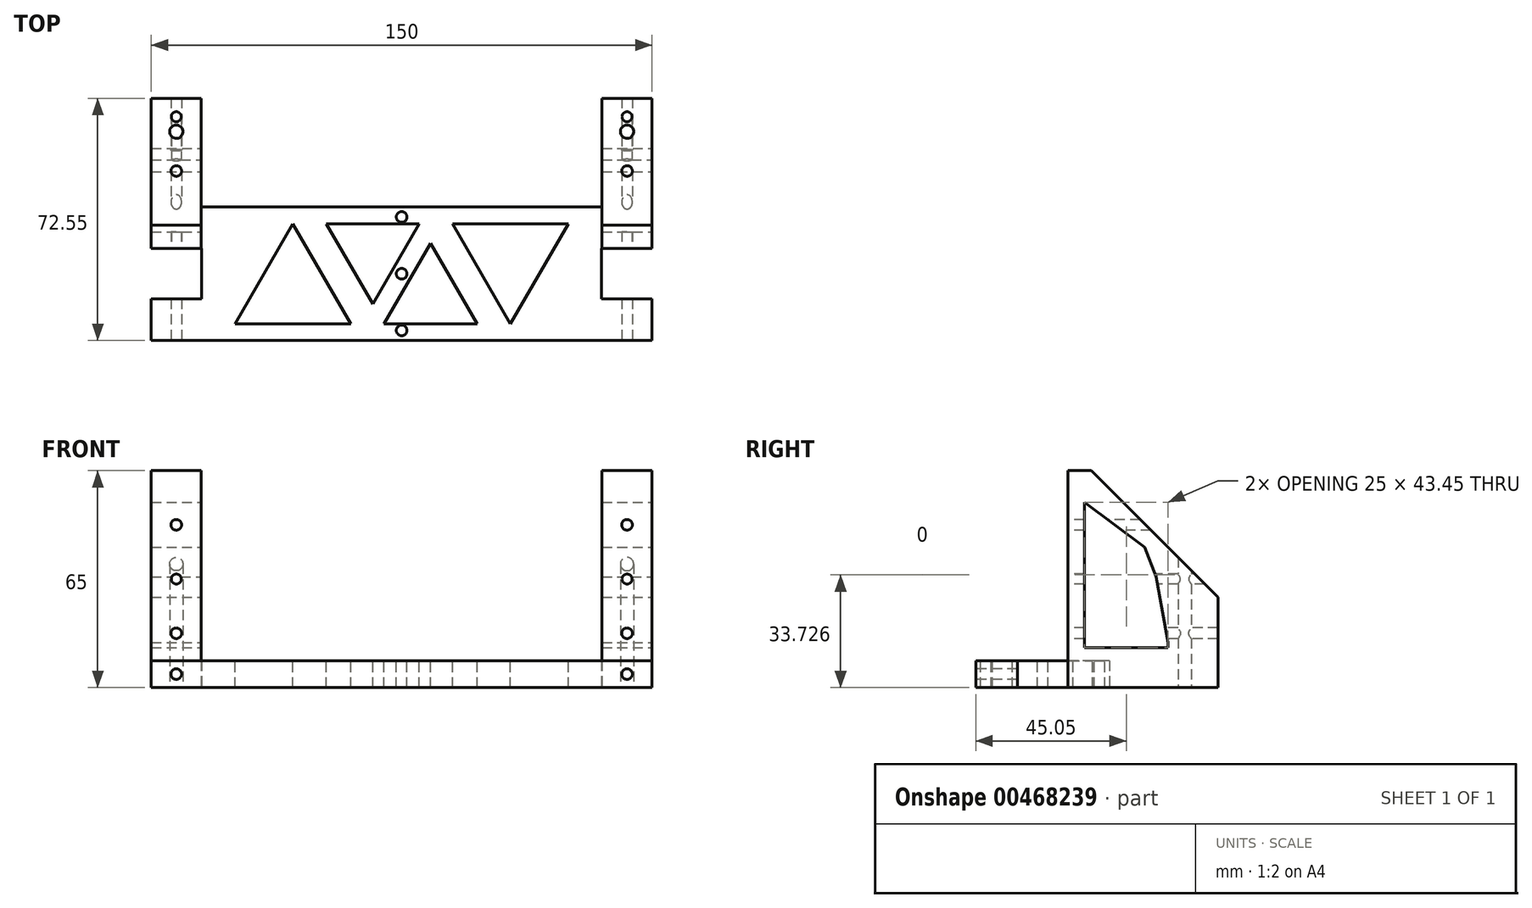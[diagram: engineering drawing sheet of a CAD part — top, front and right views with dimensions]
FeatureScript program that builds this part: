
annotation { "Feature Type Name" : "Feature", "Feature Type Description" : "" }
export const myFeature = defineFeature(function(context is Context, id is Id, definition is map)
    precondition{}
    {
        {
            var Q0;
            Q0=qCreatedBy(makeId("Top.planeOp"),FACE);
            var sketch = newSketch(context, id + "F0", { "sketchPlane" : qUnion([Q0])});
            skLineSegment(sketch, "E0.bottom", {"start": v(75, 20) * mm, "end": v(-75, 20) * mm});
            skLineSegment(sketch, "E0.top", {"start": v(75, -20) * mm, "end": v(-75, -20) * mm});
            skLineSegment(sketch, "E0.left", {"start": v(75, 20) * mm, "end": v(75, -20) * mm});
            skLineSegment(sketch, "E0.right", {"start": v(-75, 20) * mm, "end": v(-75, -20) * mm});
            skPoint(sketch, "E0.middle", {"position": v(0, 0) * mm});
            skLineSegment(sketch, "E1", {"start": v(-75, 0) * mm, "end": v(-67.45, 0) * mm});
            skLineSegment(sketch, "E2", {"start": v(75, 0) * mm, "end": v(67.45, 0) * mm});
            skLineSegment(sketch, "E3.bottom", {"start": v(75, 7.55) * mm, "end": v(59.9, 7.55) * mm});
            skLineSegment(sketch, "E3.top", {"start": v(75, -7.55) * mm, "end": v(59.9, -7.55) * mm});
            skLineSegment(sketch, "E3.left", {"start": v(75, 7.55) * mm, "end": v(75, -7.55) * mm});
            skLineSegment(sketch, "E3.right", {"start": v(59.9, 7.55) * mm, "end": v(59.9, -7.55) * mm});
            skPoint(sketch, "E3.middle", {"position": v(67.45, 0) * mm});
            skLineSegment(sketch, "E4.bottom", {"start": v(-59.9, 7.55) * mm, "end": v(-75, 7.55) * mm});
            skLineSegment(sketch, "E4.top", {"start": v(-59.9, -7.55) * mm, "end": v(-75, -7.55) * mm});
            skLineSegment(sketch, "E4.left", {"start": v(-59.9, 7.55) * mm, "end": v(-59.9, -7.55) * mm});
            skLineSegment(sketch, "E4.right", {"start": v(-75, 7.55) * mm, "end": v(-75, -7.55) * mm});
            skPoint(sketch, "E4.middle", {"position": v(-67.45, 0) * mm});
            skSolve(sketch);
        }
        {
            var Q0;
            {var subQ6=sQuery(id+"F0.wireOp",EDGE,"E0.bottom");Q0=makeQuery(id+"F0.imprint","IMPRINT",FACE,{"disambiguationData":[TD([[makeQuery(id+"F0.imprint","IMPRINT",EDGE,{"derivedFrom":subQ6}),1.0]])]});}
            extrude(context, id + "F1", {"entities" : qUnion([Q0]), "depth" : 8 * mm});
        }
        {
            var Q0;
            Q0=makeQuery(id+"F1.opExtrude","CAP_FACE",FACE,{"disambiguationData":[OSD([sQuery(id+"F0.wireOp",EDGE,"E0.bottom"),sQuery(id+"F0.wireOp",EDGE,"E0.top"),sQuery(id+"F0.wireOp",EDGE,"E0.left"),sQuery(id+"F0.wireOp",EDGE,"E0.right"),sQuery(id+"F0.wireOp",EDGE,"E3.bottom"),sQuery(id+"F0.wireOp",EDGE,"E3.top"),sQuery(id+"F0.wireOp",EDGE,"E3.right"),sQuery(id+"F0.wireOp",EDGE,"E4.bottom"),sQuery(id+"F0.wireOp",EDGE,"E4.top"),sQuery(id+"F0.wireOp",EDGE,"E4.left")])],"isStart":false});
            var sketch = newSketch(context, id + "F2", { "sketchPlane" : qUnion([Q0])});
            skLineSegment(sketch, "E5", {"start": v(0, 20) * mm, "end": v(0, 17) * mm});
            skPoint(sketch, "E5.endSnap0", {"position": v(0, 20) * mm});
            skLineSegment(sketch, "E6", {"start": v(0, -20) * mm, "end": v(0, -17) * mm});
            skPoint(sketch, "E6.endSnap0", {"position": v(0, -20) * mm});
            skCircle(sketch, "E7", {"center": v(0, -17) * mm, "radius": 1.6 * mm});
            skCircle(sketch, "E8", {"center": v(0, 0) * mm, "radius": 1.6 * mm});
            skCircle(sketch, "E9", {"center": v(0, 17) * mm, "radius": 1.6 * mm});
            skSolve(sketch);
        }
        {
            var Q0;
            Q0 = qSketchRegion(id + "F2", true);
            extrude(context, id + "F3", {"entities" : qUnion([Q0]), "operationType" : NewBodyOperationType.REMOVE, "oppositeDirection" : true, "depth" : 25 * mm});
        }
        {
            var Q0;
            Q0=makeQuery(id+"F1.opExtrude","CAP_FACE",FACE,{"disambiguationData":[OSD([sQuery(id+"F0.wireOp",EDGE,"E0.bottom"),sQuery(id+"F0.wireOp",EDGE,"E0.top"),sQuery(id+"F0.wireOp",EDGE,"E0.left"),sQuery(id+"F0.wireOp",EDGE,"E0.right"),sQuery(id+"F0.wireOp",EDGE,"E3.bottom"),sQuery(id+"F0.wireOp",EDGE,"E3.top"),sQuery(id+"F0.wireOp",EDGE,"E3.right"),sQuery(id+"F0.wireOp",EDGE,"E4.bottom"),sQuery(id+"F0.wireOp",EDGE,"E4.top"),sQuery(id+"F0.wireOp",EDGE,"E4.left")])],"isStart":true});
            var sketch = newSketch(context, id + "F4", { "sketchPlane" : qUnion([Q0])});
            skLineSegment(sketch, "E10.bottom", {"start": v(-75, -7.55) * mm, "end": v(-60, -7.55) * mm});
            skLineSegment(sketch, "E10.top", {"start": v(-75, -52.55) * mm, "end": v(-60, -52.55) * mm});
            skLineSegment(sketch, "E10.left", {"start": v(-75, -7.55) * mm, "end": v(-75, -52.55) * mm});
            skLineSegment(sketch, "E10.right", {"start": v(-60, -7.55) * mm, "end": v(-60, -52.55) * mm});
            skLineSegment(sketch, "E11.bottom", {"start": v(75, -7.55) * mm, "end": v(60, -7.55) * mm});
            skLineSegment(sketch, "E11.top", {"start": v(75, -52.55) * mm, "end": v(60, -52.55) * mm});
            skLineSegment(sketch, "E11.left", {"start": v(75, -7.55) * mm, "end": v(75, -52.55) * mm});
            skLineSegment(sketch, "E11.right", {"start": v(60, -7.55) * mm, "end": v(60, -52.55) * mm});
            skLineSegment(sketch, "E12", {"start": v(-67.5, -52.55) * mm, "end": v(-67.5, -42.55) * mm});
            skLineSegment(sketch, "E13", {"start": v(67.5, -52.55) * mm, "end": v(67.5, -42.55) * mm});
            skCircle(sketch, "E14", {"center": v(67.5, -42.55) * mm, "radius": 2 * mm});
            skCircle(sketch, "E15", {"center": v(-67.5, -42.55) * mm, "radius": 2 * mm});
            skSolve(sketch);
        }
        {
            var Q0;
            Q0=makeQuery(id+"F4.imprint","IMPRINT",FACE,{"disambiguationData":[TD([[makeQuery(id+"F4.imprint","IMPRINT",EDGE,{"derivedFrom":sQuery(id+"F4.wireOp",EDGE,"E15")}),-1.0]])]});
            var Q1;
            Q1=makeQuery(id+"F4.imprint","IMPRINT",FACE,{"disambiguationData":[TD([[makeQuery(id+"F4.imprint","IMPRINT",EDGE,{"derivedFrom":sQuery(id+"F4.wireOp",EDGE,"E14")}),-1.0]])]});
            var Q2;
            {var subQ0=sQuery(id+"F4.wireOp",EDGE,"E11.bottom");Q2=makeQuery(id+"F4.imprint","IMPRINT",FACE,{"disambiguationData":[TD([[makeQuery(id+"F4.imprint","IMPRINT",EDGE,{"derivedFrom":subQ0}),1.0]])]});}
            var Q3;
            {var subQ0=sQuery(id+"F4.wireOp",EDGE,"E10.bottom");Q3=makeQuery(id+"F4.imprint","IMPRINT",FACE,{"disambiguationData":[TD([[makeQuery(id+"F4.imprint","IMPRINT",EDGE,{"derivedFrom":subQ0}),1.0]])]});}
            extrude(context, id + "F5", {"entities" : qUnion([Q0, Q1, Q2, Q3]), "operationType" : NewBodyOperationType.ADD, "oppositeDirection" : true, "depth" : 65 * mm});
        }
        {
            var Q0;
            Q0=makeQuery(id+"F5.opExtrude","CAP_EDGE",EDGE,{"disambiguationData":[OSD([sQuery(id+"F4.wireOp",EDGE,"E11.top")])],"isStart":false});
            var Q1;
            Q1=makeQuery(id+"F5.opExtrude","CAP_EDGE",EDGE,{"disambiguationData":[OSD([sQuery(id+"F4.wireOp",EDGE,"E10.top")])],"isStart":false});
            chamfer(context, id + "F6", {"entities" : qUnion([Q0, Q1]), "width" : 38 * mm, "tangentPropagation" : true});
        }
        {
            var Q0;
            {var subQ0=sQuery(id+"F0.wireOp",EDGE,"E0.left");Q0=makeQuery(id+"F5.boolean.opBoolean","MERGE",FACE,{"derivedFrom":[makeQuery(id+"F1.opExtrude","SWEPT_FACE",FACE,{"disambiguationData":[OSD([subQ0]),TDD([makeQuery(id+"F0.imprint","IMPRINT",EDGE,{"disambiguationData":[TD([[makeQuery(id+"F0.imprint","INTERSECT",VERTEX,{"derivedFrom":[sQuery(id+"F0.wireOp",EDGE,"E0.bottom"),subQ0]}),-1.0]])],"derivedFrom":subQ0})])]}),makeQuery(id+"F5.opExtrude","SWEPT_FACE",FACE,{"disambiguationData":[OSD([sQuery(id+"F4.wireOp",EDGE,"E11.left")])]})]});}
            var sketch = newSketch(context, id + "F7", { "sketchPlane" : qUnion([Q0])});
            skLineSegment(sketch, "E16", {"start": v(30.05, 0) * mm, "end": v(30.05, 12) * mm});
            skLineSegment(sketch, "E17", {"start": v(33.55, 46) * mm, "end": v(30.56, 42) * mm});
            skLineSegment(sketch, "E18", {"start": v(7.55, 32.5) * mm, "end": v(12.55, 32.5) * mm});
            skLineSegment(sketch, "E19", {"start": v(52.55, 13.5) * mm, "end": v(37.55, 13.5) * mm});
            skLineSegment(sketch, "E20", {"start": v(30.05, 12) * mm, "end": v(7.55, 12) * mm});
            skLineSegment(sketch, "E21", {"start": v(12.55, 32.5) * mm, "end": v(12.55, 12) * mm});
            skLineSegment(sketch, "E22", {"start": v(30.05, 12) * mm, "end": v(52.55, 12) * mm});
            skLineSegment(sketch, "E23", {"start": v(30.56, 42) * mm, "end": v(52.55, 25.56) * mm});
            skLineSegment(sketch, "E24", {"start": v(37.55, 13.5) * mm, "end": v(37.55, 12) * mm});
            skLineSegment(sketch, "E25", {"start": v(37.55, 12) * mm, "end": v(37.55, 36.77) * mm});
            skLineSegment(sketch, "E26", {"start": v(11.05, 65) * mm, "end": v(11.05, 60) * mm});
            skLineSegment(sketch, "E27", {"start": v(11.05, 60) * mm, "end": v(19.55, 60) * mm});
            skLineSegment(sketch, "E28", {"start": v(11.05, 60) * mm, "end": v(7.55, 60) * mm});
            skLineSegment(sketch, "E29", {"start": v(12.55, 32.5) * mm, "end": v(12.55, 60) * mm});
            skLineSegment(sketch, "E30", {"start": v(30.56, 42) * mm, "end": v(12.55, 55.45) * mm});
            skLineSegment(sketch, "E31", {"start": v(30.56, 42) * mm, "end": v(37.55, 24.38) * mm});
            skLineSegment(sketch, "E32", {"start": v(34.05, 33.19) * mm, "end": v(37.55, 13.5) * mm});
            skSolve(sketch);
        }
        {
            var Q0;
            {var subQ5=sQuery(id+"F7.wireOp",EDGE,"E21");Q0=makeQuery(id+"F7.imprint","IMPRINT",FACE,{"disambiguationData":[TD([[makeQuery(id+"F7.imprint","IMPRINT",EDGE,{"derivedFrom":subQ5}),1.0]])]});}
            extrude(context, id + "F8", {"entities" : qUnion([Q0]), "operationType" : NewBodyOperationType.REMOVE, "oppositeDirection" : true, "depth" : 200 * mm});
        }
        {
            var Q0;
            Q0=qCreatedBy(makeId("Front.planeOp"),FACE);
            var sketch = newSketch(context, id + "F9", { "sketchPlane" : qUnion([Q0])});
            skLineSegment(sketch, "E33", {"start": v(0, 0) * mm, "end": v(0, 65) * mm});
            skLineSegment(sketch, "E34", {"start": v(0, 0) * mm, "end": v(0, 32.5) * mm});
            skLineSegment(sketch, "E35", {"start": v(0, 16.25) * mm, "end": v(67.5, 16.25) * mm});
            skPoint(sketch, "E35.endSnap0", {"position": v(0, 16.25) * mm});
            skLineSegment(sketch, "E36", {"start": v(0, 32.5) * mm, "end": v(67.5, 32.5) * mm});
            skLineSegment(sketch, "E37", {"start": v(0, 65) * mm, "end": v(0, 32.5) * mm});
            skLineSegment(sketch, "E38", {"start": v(0, 48.75) * mm, "end": v(67.5, 48.75) * mm});
            skLineSegment(sketch, "E39", {"start": v(0, 48.75) * mm, "end": v(-67.5, 48.75) * mm});
            skLineSegment(sketch, "E40", {"start": v(0, 32.5) * mm, "end": v(-67.5, 32.5) * mm});
            skLineSegment(sketch, "E41", {"start": v(0, 16.25) * mm, "end": v(-67.5, 16.25) * mm});
            skCircle(sketch, "E42", {"center": v(-67.5, 48.75) * mm, "radius": 1.6 * mm});
            skCircle(sketch, "E43", {"center": v(-67.5, 32.5) * mm, "radius": 1.5 * mm});
            skCircle(sketch, "E44", {"center": v(-67.5, 16.25) * mm, "radius": 1.6 * mm});
            skCircle(sketch, "E45", {"center": v(67.5, 32.5) * mm, "radius": 1.5 * mm});
            skCircle(sketch, "E46", {"center": v(67.5, 16.25) * mm, "radius": 1.6 * mm});
            skCircle(sketch, "E47", {"center": v(67.5, 48.75) * mm, "radius": 1.6 * mm});
            skSolve(sketch);
        }
        {
            var Q0;
            Q0 = qSketchRegion(id + "F9", true);
            extrude(context, id + "F10", {"entities" : qUnion([Q0]), "operationType" : NewBodyOperationType.REMOVE, "oppositeDirection" : true, "depth" : 1000 * mm});
        }
        {
            var Q0;
            Q0=makeQuery(id+"F1.opExtrude","CAP_FACE",FACE,{"disambiguationData":[OSD([sQuery(id+"F0.wireOp",EDGE,"E0.bottom"),sQuery(id+"F0.wireOp",EDGE,"E0.top"),sQuery(id+"F0.wireOp",EDGE,"E0.left"),sQuery(id+"F0.wireOp",EDGE,"E0.right"),sQuery(id+"F0.wireOp",EDGE,"E3.bottom"),sQuery(id+"F0.wireOp",EDGE,"E3.top"),sQuery(id+"F0.wireOp",EDGE,"E3.right"),sQuery(id+"F0.wireOp",EDGE,"E4.bottom"),sQuery(id+"F0.wireOp",EDGE,"E4.top"),sQuery(id+"F0.wireOp",EDGE,"E4.left")])],"isStart":false});
            var sketch = newSketch(context, id + "F11", { "sketchPlane" : qUnion([Q0])});
            skLineSegment(sketch, "E48", {"start": v(-59.9, 0) * mm, "end": v(-49.9, 0) * mm});
            skLineSegment(sketch, "E49", {"start": v(59.9, 0) * mm, "end": v(49.9, 0) * mm});
            skPoint(sketch, "E49.endSnap0", {"position": v(59.9, 0) * mm});
            skLineSegment(sketch, "E50", {"start": v(-49.9, 0) * mm, "end": v(-49.9, 20) * mm});
            skLineSegment(sketch, "E51", {"start": v(-49.9, 0) * mm, "end": v(-49.9, -20) * mm});
            skLineSegment(sketch, "E52", {"start": v(-49.9, -20) * mm, "end": v(-49.9, -15) * mm});
            skLineSegment(sketch, "E53", {"start": v(-49.9, 20) * mm, "end": v(-49.9, 15) * mm});
            skLineSegment(sketch, "E54", {"start": v(-49.9, 15) * mm, "end": v(60, 15) * mm});
            skLineSegment(sketch, "E55", {"start": v(-49.9, -15) * mm, "end": v(75, -15) * mm});
            skLineSegment(sketch, "E56", {"start": v(-49.9, -15) * mm, "end": v(-36.64, 7.96) * mm});
            skLineSegment(sketch, "E57", {"start": v(-49.9, -15) * mm, "end": v(-32.58, 15) * mm});
            skLineSegment(sketch, "E58", {"start": v(-32.58, 15) * mm, "end": v(-15.26, -15) * mm});
            skLineSegment(sketch, "E59", {"start": v(60, 15) * mm, "end": v(60, -15) * mm});
            skLineSegment(sketch, "E60", {"start": v(-32.58, 15) * mm, "end": v(-22.58, 15) * mm});
            skLineSegment(sketch, "E61", {"start": v(-22.58, 15) * mm, "end": v(-5.26, -15) * mm});
            skLineSegment(sketch, "E62", {"start": v(-5.26, -15) * mm, "end": v(12.06, 15) * mm});
            skLineSegment(sketch, "E63", {"start": v(49.9, 0) * mm, "end": v(49.9, 20) * mm});
            skLineSegment(sketch, "E64", {"start": v(49.9, 0) * mm, "end": v(49.9, -20) * mm});
            skLineSegment(sketch, "E65", {"start": v(-5.26, -15) * mm, "end": v(4.74, -15) * mm});
            skLineSegment(sketch, "E66", {"start": v(49.9, 15) * mm, "end": v(32.58, -15) * mm});
            skLineSegment(sketch, "E67", {"start": v(32.58, -15) * mm, "end": v(15.26, 15) * mm});
            skLineSegment(sketch, "E68", {"start": v(32.58, -15) * mm, "end": v(22.58, -15) * mm});
            skLineSegment(sketch, "E69", {"start": v(22.58, -15) * mm, "end": v(5.26, 15) * mm});
            skLineSegment(sketch, "E70", {"start": v(5.26, 15) * mm, "end": v(-12.06, -15) * mm});
            skSolve(sketch);
        }
        {
            var Q0;
            {var subQ3=sQuery(id+"F11.wireOp",EDGE,"E58");Q0=makeQuery(id+"F11.imprint","IMPRINT",FACE,{"disambiguationData":[TD([[makeQuery(id+"F11.imprint","IMPRINT",EDGE,{"derivedFrom":subQ3}),-1.0]])]});}
            var Q1;
            {var subQ0=sQuery(id+"F11.wireOp",EDGE,"E61");Q1=makeQuery(id+"F11.imprint","IMPRINT",FACE,{"disambiguationData":[TD([[makeQuery(id+"F11.imprint","IMPRINT",EDGE,{"derivedFrom":subQ0}),1.0]])]});}
            var Q2;
            {var subQ0=sQuery(id+"F11.wireOp",EDGE,"E69");Q2=makeQuery(id+"F11.imprint","IMPRINT",FACE,{"disambiguationData":[TD([[makeQuery(id+"F11.imprint","IMPRINT",EDGE,{"derivedFrom":subQ0}),1.0]])]});}
            var Q3;
            {var subQ0=sQuery(id+"F11.wireOp",EDGE,"E66");Q3=makeQuery(id+"F11.imprint","IMPRINT",FACE,{"disambiguationData":[TD([[makeQuery(id+"F11.imprint","IMPRINT",EDGE,{"derivedFrom":subQ0}),-1.0]])]});}
            extrude(context, id + "F12", {"entities" : qUnion([Q0, Q1, Q2, Q3]), "operationType" : NewBodyOperationType.REMOVE, "oppositeDirection" : true, "depth" : 25 * mm});
        }
        {
            var Q0;
            Q0=makeQuery(id+"F1.opExtrude","SWEPT_FACE",FACE,{"disambiguationData":[OSD([sQuery(id+"F0.wireOp",EDGE,"E0.top")])]});
            var sketch = newSketch(context, id + "F13", { "sketchPlane" : qUnion([Q0])});
            skLineSegment(sketch, "E71", {"start": v(-75, 4) * mm, "end": v(-67.5, 4) * mm});
            skLineSegment(sketch, "E72", {"start": v(75, 4) * mm, "end": v(67.5, 4) * mm});
            skCircle(sketch, "E73", {"center": v(-67.5, 4) * mm, "radius": 1.6 * mm});
            skCircle(sketch, "E74", {"center": v(67.5, 4) * mm, "radius": 1.6 * mm});
            skSolve(sketch);
        }
        {
            var Q0;
            Q0 = qSketchRegion(id + "F13", true);
            extrude(context, id + "F14", {"entities" : qUnion([Q0]), "operationType" : NewBodyOperationType.REMOVE, "oppositeDirection" : true, "depth" : 12.5 * mm});
        }
    });
